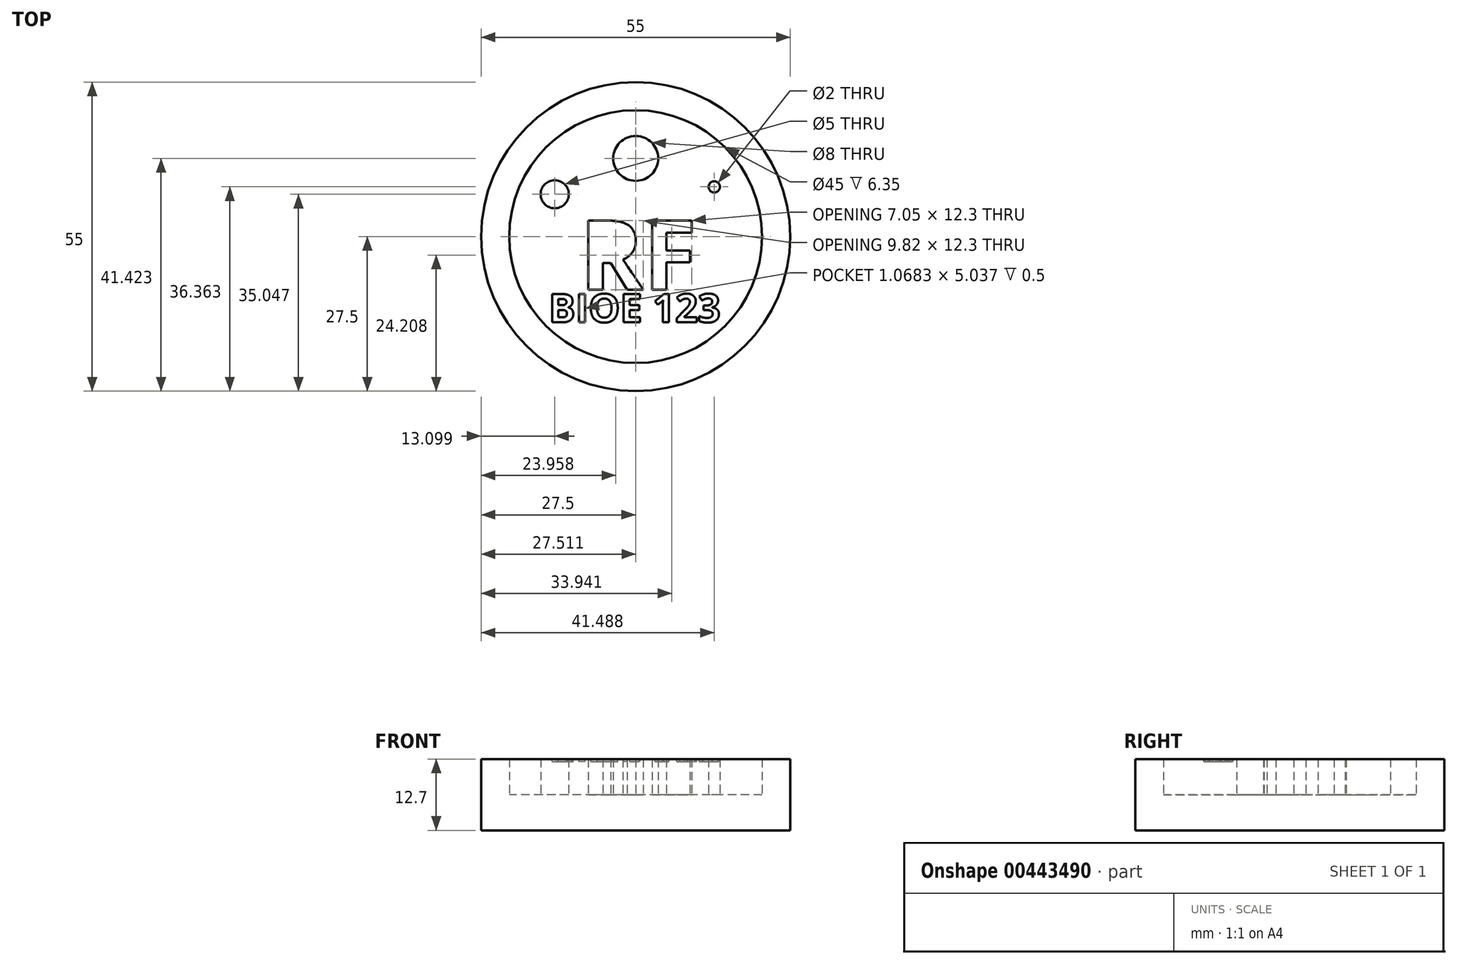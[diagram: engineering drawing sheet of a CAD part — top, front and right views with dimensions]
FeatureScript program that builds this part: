
annotation { "Feature Type Name" : "Feature", "Feature Type Description" : "" }
export const myFeature = defineFeature(function(context is Context, id is Id, definition is map)
    precondition{}
    {
        {
            var Q0;
            Q0=qCreatedBy(makeId("Top.planeOp"),FACE);
            var sketch = newSketch(context, id + "F0", { "sketchPlane" : qUnion([Q0])});
            skCircle(sketch, "E0", {"center": v(0, 0) * mm, "radius": 22.5 * mm});
            skCircle(sketch, "E1", {"center": v(0, 0) * mm, "radius": 27.5 * mm});
            skCircle(sketch, "E2", {"center": v(0.01, 13.92) * mm, "radius": 4 * mm});
            skCircle(sketch, "E3", {"center": v(-14.4, 7.55) * mm, "radius": 2.5 * mm});
            skCircle(sketch, "E4", {"center": v(13.99, 8.86) * mm, "radius": 1 * mm});
            skText(sketch, "E5", { "text": "RF", "fontName": "OpenSans-Bold.ttf"});
            const initialGuessF0  = {"E5": [-0.01, -0.00944, 1, 0, 0.0124]};
            skSetInitialGuess(sketch, initialGuessF0);
            skSolve(sketch);
        }
        {
            var Q0;
            Q0=makeQuery(id+"F0.imprint","IMPRINT",FACE,{"disambiguationData":[TD([[makeQuery(id+"F0.imprint","IMPRINT",EDGE,{"derivedFrom":sQuery(id+"F0.wireOp",EDGE,"E2")}),1.0]])]});
            var Q1;
            Q1=makeQuery(id+"F0.imprint","IMPRINT",FACE,{"disambiguationData":[TD([[makeQuery(id+"F0.imprint","IMPRINT",EDGE,{"derivedFrom":sQuery(id+"F0.wireOp",EDGE,"E4")}),1.0]])]});
            var Q2;
            Q2=makeQuery(id+"F0.imprint","IMPRINT",FACE,{"disambiguationData":[TD([[makeQuery(id+"F0.imprint","IMPRINT",EDGE,{"derivedFrom":sQuery(id+"F0.wireOp",EDGE,"E3")}),1.0]])]});
            var Q3;
            Q3=makeQuery(id+"F0.imprint","IMPRINT",FACE,{"disambiguationData":[TD([[makeQuery(id+"F0.imprint","IMPRINT",EDGE,{"derivedFrom":sQuery(id+"F0.wireOp",EDGE,"949e2ff5-e721-49a0-989e-4c56e190631b.sketch_text.stroke-0")}),-1.0]])]});
            var Q4;
            Q4=makeQuery(id+"F0.imprint","IMPRINT",FACE,{"disambiguationData":[TD([[makeQuery(id+"F0.imprint","IMPRINT",EDGE,{"derivedFrom":sQuery(id+"F0.wireOp",EDGE,"949e2ff5-e721-49a0-989e-4c56e190631b.sketch_text.stroke-26")}),-1.0]])]});
            var Q5;
            Q5=makeQuery(id+"F0.imprint","IMPRINT",FACE,{"disambiguationData":[TD([[makeQuery(id+"F0.imprint","IMPRINT",EDGE,{"derivedFrom":sQuery(id+"F0.wireOp",EDGE,"949e2ff5-e721-49a0-989e-4c56e190631b.sketch_text.stroke-19")}),-1.0]])]});
            var Q6;
            Q6=makeQuery(id+"F0.imprint","IMPRINT",FACE,{"disambiguationData":[TD([[makeQuery(id+"F0.imprint","IMPRINT",EDGE,{"derivedFrom":sQuery(id+"F0.wireOp",EDGE,"949e2ff5-e721-49a0-989e-4c56e190631b.sketch_text.stroke-36")}),-1.0]])]});
            var Q7;
            Q7=makeQuery(id+"F0.imprint","IMPRINT",FACE,{"disambiguationData":[TD([[makeQuery(id+"F0.imprint","IMPRINT",EDGE,{"derivedFrom":sQuery(id+"F0.wireOp",EDGE,"949e2ff5-e721-49a0-989e-4c56e190631b.sketch_text.stroke-40")}),-1.0]])]});
            var Q8;
            Q8=makeQuery(id+"F0.imprint","IMPRINT",FACE,{"disambiguationData":[TD([[makeQuery(id+"F0.imprint","IMPRINT",EDGE,{"derivedFrom":sQuery(id+"F0.wireOp",EDGE,"949e2ff5-e721-49a0-989e-4c56e190631b.sketch_text.stroke-48")}),-1.0]])]});
            var Q9;
            Q9=makeQuery(id+"F0.imprint","IMPRINT",FACE,{"disambiguationData":[TD([[makeQuery(id+"F0.imprint","IMPRINT",EDGE,{"derivedFrom":sQuery(id+"F0.wireOp",EDGE,"949e2ff5-e721-49a0-989e-4c56e190631b.sketch_text.stroke-110")}),-1.0]])]});
            var Q10;
            Q10=makeQuery(id+"F0.imprint","IMPRINT",FACE,{"disambiguationData":[TD([[makeQuery(id+"F0.imprint","IMPRINT",EDGE,{"derivedFrom":sQuery(id+"F0.wireOp",EDGE,"949e2ff5-e721-49a0-989e-4c56e190631b.sketch_text.stroke-122")}),-1.0]])]});
            var Q11;
            Q11=makeQuery(id+"F0.imprint","IMPRINT",FACE,{"disambiguationData":[TD([[makeQuery(id+"F0.imprint","IMPRINT",EDGE,{"derivedFrom":sQuery(id+"F0.wireOp",EDGE,"949e2ff5-e721-49a0-989e-4c56e190631b.sketch_text.stroke-100")}),-1.0]])]});
            var Q12;
            Q12=makeQuery(id+"F0.imprint","IMPRINT",FACE,{"disambiguationData":[TD([[makeQuery(id+"F0.imprint","IMPRINT",EDGE,{"derivedFrom":sQuery(id+"F0.wireOp",EDGE,"949e2ff5-e721-49a0-989e-4c56e190631b.sketch_text.stroke-88")}),-1.0]])]});
            var Q13;
            Q13=makeQuery(id+"F0.imprint","IMPRINT",FACE,{"disambiguationData":[TD([[makeQuery(id+"F0.imprint","IMPRINT",EDGE,{"derivedFrom":sQuery(id+"F0.wireOp",EDGE,"949e2ff5-e721-49a0-989e-4c56e190631b.sketch_text.stroke-92")}),-1.0]])]});
            var Q14;
            Q14=makeQuery(id+"F0.imprint","IMPRINT",FACE,{"disambiguationData":[TD([[makeQuery(id+"F0.imprint","IMPRINT",EDGE,{"derivedFrom":sQuery(id+"F0.wireOp",EDGE,"949e2ff5-e721-49a0-989e-4c56e190631b.sketch_text.stroke-63")}),-1.0]])]});
            var Q15;
            Q15=makeQuery(id+"F0.imprint","IMPRINT",FACE,{"disambiguationData":[TD([[makeQuery(id+"F0.imprint","IMPRINT",EDGE,{"derivedFrom":sQuery(id+"F0.wireOp",EDGE,"E5.sketch_text.stroke-0")}),1.0]])]});
            var Q16;
            Q16=makeQuery(id+"F0.imprint","IMPRINT",FACE,{"disambiguationData":[TD([[makeQuery(id+"F0.imprint","IMPRINT",EDGE,{"derivedFrom":sQuery(id+"F0.wireOp",EDGE,"E5.sketch_text.stroke-0")}),-1.0]])]});
            var Q17;
            Q17=makeQuery(id+"F0.imprint","IMPRINT",FACE,{"disambiguationData":[TD([[makeQuery(id+"F0.imprint","IMPRINT",EDGE,{"derivedFrom":sQuery(id+"F0.wireOp",EDGE,"E5.sketch_text.stroke-19")}),-1.0]])]});
            extrude(context, id + "F1", {"entities" : qUnion([Q0, Q1, Q2, Q3, Q4, Q5, Q6, Q7, Q8, Q9, Q10, Q11, Q12, Q13, Q14, Q15, Q16, Q17]), "depth" : 12.7 * mm});
        }
        {
            var Q0;
            Q0 = qSketchRegion(id + "F0", true);
            extrude(context, id + "F2", {"entities" : qUnion([Q0]), "operationType" : NewBodyOperationType.ADD, "depth" : 12.7 * mm});
        }
        {
            var Q0;
            Q0=makeQuery(id+"F0.imprint","IMPRINT",FACE,{"disambiguationData":[TD([[makeQuery(id+"F0.imprint","IMPRINT",EDGE,{"derivedFrom":sQuery(id+"F0.wireOp",EDGE,"E0")}),1.0]])]});
            extrude(context, id + "F3", {"entities" : qUnion([Q0]), "operationType" : NewBodyOperationType.ADD, "depth" : 6.35 * mm});
        }
        {
            var Q0;
            Q0=makeQuery(id+"F3.opExtrude","CAP_FACE",FACE,{"disambiguationData":[OSD([sQuery(id+"F0.wireOp",EDGE,"E0"),sQuery(id+"F0.wireOp",EDGE,"E2"),sQuery(id+"F0.wireOp",EDGE,"E3"),sQuery(id+"F0.wireOp",EDGE,"E4"),sQuery(id+"F0.wireOp",EDGE,"949e2ff5-e721-49a0-989e-4c56e190631b.sketch_text.stroke-0"),sQuery(id+"F0.wireOp",EDGE,"949e2ff5-e721-49a0-989e-4c56e190631b.sketch_text.stroke-1"),sQuery(id+"F0.wireOp",EDGE,"949e2ff5-e721-49a0-989e-4c56e190631b.sketch_text.stroke-2"),sQuery(id+"F0.wireOp",EDGE,"949e2ff5-e721-49a0-989e-4c56e190631b.sketch_text.stroke-3"),sQuery(id+"F0.wireOp",EDGE,"949e2ff5-e721-49a0-989e-4c56e190631b.sketch_text.stroke-4"),sQuery(id+"F0.wireOp",EDGE,"949e2ff5-e721-49a0-989e-4c56e190631b.sketch_text.stroke-5"),sQuery(id+"F0.wireOp",EDGE,"949e2ff5-e721-49a0-989e-4c56e190631b.sketch_text.stroke-6"),sQuery(id+"F0.wireOp",EDGE,"949e2ff5-e721-49a0-989e-4c56e190631b.sketch_text.stroke-7"),sQuery(id+"F0.wireOp",EDGE,"949e2ff5-e721-49a0-989e-4c56e190631b.sketch_text.stroke-8"),sQuery(id+"F0.wireOp",EDGE,"949e2ff5-e721-49a0-989e-4c56e190631b.sketch_text.stroke-9"),sQuery(id+"F0.wireOp",EDGE,"949e2ff5-e721-49a0-989e-4c56e190631b.sketch_text.stroke-10"),sQuery(id+"F0.wireOp",EDGE,"949e2ff5-e721-49a0-989e-4c56e190631b.sketch_text.stroke-11"),sQuery(id+"F0.wireOp",EDGE,"949e2ff5-e721-49a0-989e-4c56e190631b.sketch_text.stroke-12"),sQuery(id+"F0.wireOp",EDGE,"949e2ff5-e721-49a0-989e-4c56e190631b.sketch_text.stroke-13"),sQuery(id+"F0.wireOp",EDGE,"949e2ff5-e721-49a0-989e-4c56e190631b.sketch_text.stroke-19"),sQuery(id+"F0.wireOp",EDGE,"949e2ff5-e721-49a0-989e-4c56e190631b.sketch_text.stroke-20"),sQuery(id+"F0.wireOp",EDGE,"949e2ff5-e721-49a0-989e-4c56e190631b.sketch_text.stroke-21"),sQuery(id+"F0.wireOp",EDGE,"949e2ff5-e721-49a0-989e-4c56e190631b.sketch_text.stroke-22"),sQuery(id+"F0.wireOp",EDGE,"949e2ff5-e721-49a0-989e-4c56e190631b.sketch_text.stroke-23"),sQuery(id+"F0.wireOp",EDGE,"949e2ff5-e721-49a0-989e-4c56e190631b.sketch_text.stroke-24"),sQuery(id+"F0.wireOp",EDGE,"949e2ff5-e721-49a0-989e-4c56e190631b.sketch_text.stroke-25"),sQuery(id+"F0.wireOp",EDGE,"949e2ff5-e721-49a0-989e-4c56e190631b.sketch_text.stroke-26"),sQuery(id+"F0.wireOp",EDGE,"949e2ff5-e721-49a0-989e-4c56e190631b.sketch_text.stroke-27"),sQuery(id+"F0.wireOp",EDGE,"949e2ff5-e721-49a0-989e-4c56e190631b.sketch_text.stroke-28"),sQuery(id+"F0.wireOp",EDGE,"949e2ff5-e721-49a0-989e-4c56e190631b.sketch_text.stroke-29"),sQuery(id+"F0.wireOp",EDGE,"949e2ff5-e721-49a0-989e-4c56e190631b.sketch_text.stroke-30"),sQuery(id+"F0.wireOp",EDGE,"949e2ff5-e721-49a0-989e-4c56e190631b.sketch_text.stroke-31"),sQuery(id+"F0.wireOp",EDGE,"949e2ff5-e721-49a0-989e-4c56e190631b.sketch_text.stroke-32"),sQuery(id+"F0.wireOp",EDGE,"949e2ff5-e721-49a0-989e-4c56e190631b.sketch_text.stroke-33"),sQuery(id+"F0.wireOp",EDGE,"949e2ff5-e721-49a0-989e-4c56e190631b.sketch_text.stroke-34"),sQuery(id+"F0.wireOp",EDGE,"949e2ff5-e721-49a0-989e-4c56e190631b.sketch_text.stroke-35"),sQuery(id+"F0.wireOp",EDGE,"949e2ff5-e721-49a0-989e-4c56e190631b.sketch_text.stroke-36"),sQuery(id+"F0.wireOp",EDGE,"949e2ff5-e721-49a0-989e-4c56e190631b.sketch_text.stroke-37"),sQuery(id+"F0.wireOp",EDGE,"949e2ff5-e721-49a0-989e-4c56e190631b.sketch_text.stroke-38"),sQuery(id+"F0.wireOp",EDGE,"949e2ff5-e721-49a0-989e-4c56e190631b.sketch_text.stroke-39"),sQuery(id+"F0.wireOp",EDGE,"949e2ff5-e721-49a0-989e-4c56e190631b.sketch_text.stroke-40"),sQuery(id+"F0.wireOp",EDGE,"949e2ff5-e721-49a0-989e-4c56e190631b.sketch_text.stroke-41"),sQuery(id+"F0.wireOp",EDGE,"949e2ff5-e721-49a0-989e-4c56e190631b.sketch_text.stroke-42"),sQuery(id+"F0.wireOp",EDGE,"949e2ff5-e721-49a0-989e-4c56e190631b.sketch_text.stroke-43"),sQuery(id+"F0.wireOp",EDGE,"949e2ff5-e721-49a0-989e-4c56e190631b.sketch_text.stroke-44"),sQuery(id+"F0.wireOp",EDGE,"949e2ff5-e721-49a0-989e-4c56e190631b.sketch_text.stroke-45"),sQuery(id+"F0.wireOp",EDGE,"949e2ff5-e721-49a0-989e-4c56e190631b.sketch_text.stroke-46"),sQuery(id+"F0.wireOp",EDGE,"949e2ff5-e721-49a0-989e-4c56e190631b.sketch_text.stroke-47"),sQuery(id+"F0.wireOp",EDGE,"949e2ff5-e721-49a0-989e-4c56e190631b.sketch_text.stroke-48"),sQuery(id+"F0.wireOp",EDGE,"949e2ff5-e721-49a0-989e-4c56e190631b.sketch_text.stroke-49"),sQuery(id+"F0.wireOp",EDGE,"949e2ff5-e721-49a0-989e-4c56e190631b.sketch_text.stroke-50"),sQuery(id+"F0.wireOp",EDGE,"949e2ff5-e721-49a0-989e-4c56e190631b.sketch_text.stroke-51"),sQuery(id+"F0.wireOp",EDGE,"949e2ff5-e721-49a0-989e-4c56e190631b.sketch_text.stroke-52"),sQuery(id+"F0.wireOp",EDGE,"949e2ff5-e721-49a0-989e-4c56e190631b.sketch_text.stroke-53"),sQuery(id+"F0.wireOp",EDGE,"949e2ff5-e721-49a0-989e-4c56e190631b.sketch_text.stroke-54"),sQuery(id+"F0.wireOp",EDGE,"949e2ff5-e721-49a0-989e-4c56e190631b.sketch_text.stroke-55"),sQuery(id+"F0.wireOp",EDGE,"949e2ff5-e721-49a0-989e-4c56e190631b.sketch_text.stroke-56"),sQuery(id+"F0.wireOp",EDGE,"949e2ff5-e721-49a0-989e-4c56e190631b.sketch_text.stroke-57"),sQuery(id+"F0.wireOp",EDGE,"949e2ff5-e721-49a0-989e-4c56e190631b.sketch_text.stroke-58"),sQuery(id+"F0.wireOp",EDGE,"949e2ff5-e721-49a0-989e-4c56e190631b.sketch_text.stroke-59"),sQuery(id+"F0.wireOp",EDGE,"949e2ff5-e721-49a0-989e-4c56e190631b.sketch_text.stroke-60"),sQuery(id+"F0.wireOp",EDGE,"949e2ff5-e721-49a0-989e-4c56e190631b.sketch_text.stroke-61"),sQuery(id+"F0.wireOp",EDGE,"949e2ff5-e721-49a0-989e-4c56e190631b.sketch_text.stroke-62"),sQuery(id+"F0.wireOp",EDGE,"949e2ff5-e721-49a0-989e-4c56e190631b.sketch_text.stroke-63"),sQuery(id+"F0.wireOp",EDGE,"949e2ff5-e721-49a0-989e-4c56e190631b.sketch_text.stroke-64"),sQuery(id+"F0.wireOp",EDGE,"949e2ff5-e721-49a0-989e-4c56e190631b.sketch_text.stroke-65"),sQuery(id+"F0.wireOp",EDGE,"949e2ff5-e721-49a0-989e-4c56e190631b.sketch_text.stroke-66"),sQuery(id+"F0.wireOp",EDGE,"949e2ff5-e721-49a0-989e-4c56e190631b.sketch_text.stroke-67"),sQuery(id+"F0.wireOp",EDGE,"949e2ff5-e721-49a0-989e-4c56e190631b.sketch_text.stroke-68"),sQuery(id+"F0.wireOp",EDGE,"949e2ff5-e721-49a0-989e-4c56e190631b.sketch_text.stroke-69"),sQuery(id+"F0.wireOp",EDGE,"949e2ff5-e721-49a0-989e-4c56e190631b.sketch_text.stroke-70"),sQuery(id+"F0.wireOp",EDGE,"949e2ff5-e721-49a0-989e-4c56e190631b.sketch_text.stroke-71"),sQuery(id+"F0.wireOp",EDGE,"949e2ff5-e721-49a0-989e-4c56e190631b.sketch_text.stroke-72"),sQuery(id+"F0.wireOp",EDGE,"949e2ff5-e721-49a0-989e-4c56e190631b.sketch_text.stroke-73"),sQuery(id+"F0.wireOp",EDGE,"949e2ff5-e721-49a0-989e-4c56e190631b.sketch_text.stroke-74"),sQuery(id+"F0.wireOp",EDGE,"949e2ff5-e721-49a0-989e-4c56e190631b.sketch_text.stroke-75"),sQuery(id+"F0.wireOp",EDGE,"949e2ff5-e721-49a0-989e-4c56e190631b.sketch_text.stroke-76"),sQuery(id+"F0.wireOp",EDGE,"949e2ff5-e721-49a0-989e-4c56e190631b.sketch_text.stroke-77"),sQuery(id+"F0.wireOp",EDGE,"949e2ff5-e721-49a0-989e-4c56e190631b.sketch_text.stroke-78"),sQuery(id+"F0.wireOp",EDGE,"949e2ff5-e721-49a0-989e-4c56e190631b.sketch_text.stroke-88"),sQuery(id+"F0.wireOp",EDGE,"949e2ff5-e721-49a0-989e-4c56e190631b.sketch_text.stroke-89"),sQuery(id+"F0.wireOp",EDGE,"949e2ff5-e721-49a0-989e-4c56e190631b.sketch_text.stroke-90"),sQuery(id+"F0.wireOp",EDGE,"949e2ff5-e721-49a0-989e-4c56e190631b.sketch_text.stroke-91"),sQuery(id+"F0.wireOp",EDGE,"949e2ff5-e721-49a0-989e-4c56e190631b.sketch_text.stroke-92"),sQuery(id+"F0.wireOp",EDGE,"949e2ff5-e721-49a0-989e-4c56e190631b.sketch_text.stroke-93"),sQuery(id+"F0.wireOp",EDGE,"949e2ff5-e721-49a0-989e-4c56e190631b.sketch_text.stroke-94"),sQuery(id+"F0.wireOp",EDGE,"949e2ff5-e721-49a0-989e-4c56e190631b.sketch_text.stroke-95"),sQuery(id+"F0.wireOp",EDGE,"949e2ff5-e721-49a0-989e-4c56e190631b.sketch_text.stroke-96"),sQuery(id+"F0.wireOp",EDGE,"949e2ff5-e721-49a0-989e-4c56e190631b.sketch_text.stroke-97"),sQuery(id+"F0.wireOp",EDGE,"949e2ff5-e721-49a0-989e-4c56e190631b.sketch_text.stroke-98"),sQuery(id+"F0.wireOp",EDGE,"949e2ff5-e721-49a0-989e-4c56e190631b.sketch_text.stroke-99"),sQuery(id+"F0.wireOp",EDGE,"949e2ff5-e721-49a0-989e-4c56e190631b.sketch_text.stroke-100"),sQuery(id+"F0.wireOp",EDGE,"949e2ff5-e721-49a0-989e-4c56e190631b.sketch_text.stroke-101"),sQuery(id+"F0.wireOp",EDGE,"949e2ff5-e721-49a0-989e-4c56e190631b.sketch_text.stroke-102"),sQuery(id+"F0.wireOp",EDGE,"949e2ff5-e721-49a0-989e-4c56e190631b.sketch_text.stroke-103"),sQuery(id+"F0.wireOp",EDGE,"949e2ff5-e721-49a0-989e-4c56e190631b.sketch_text.stroke-104"),sQuery(id+"F0.wireOp",EDGE,"949e2ff5-e721-49a0-989e-4c56e190631b.sketch_text.stroke-105"),sQuery(id+"F0.wireOp",EDGE,"949e2ff5-e721-49a0-989e-4c56e190631b.sketch_text.stroke-106"),sQuery(id+"F0.wireOp",EDGE,"949e2ff5-e721-49a0-989e-4c56e190631b.sketch_text.stroke-107"),sQuery(id+"F0.wireOp",EDGE,"949e2ff5-e721-49a0-989e-4c56e190631b.sketch_text.stroke-108"),sQuery(id+"F0.wireOp",EDGE,"949e2ff5-e721-49a0-989e-4c56e190631b.sketch_text.stroke-109"),sQuery(id+"F0.wireOp",EDGE,"949e2ff5-e721-49a0-989e-4c56e190631b.sketch_text.stroke-110"),sQuery(id+"F0.wireOp",EDGE,"949e2ff5-e721-49a0-989e-4c56e190631b.sketch_text.stroke-111"),sQuery(id+"F0.wireOp",EDGE,"949e2ff5-e721-49a0-989e-4c56e190631b.sketch_text.stroke-112"),sQuery(id+"F0.wireOp",EDGE,"949e2ff5-e721-49a0-989e-4c56e190631b.sketch_text.stroke-113"),sQuery(id+"F0.wireOp",EDGE,"949e2ff5-e721-49a0-989e-4c56e190631b.sketch_text.stroke-114"),sQuery(id+"F0.wireOp",EDGE,"949e2ff5-e721-49a0-989e-4c56e190631b.sketch_text.stroke-115"),sQuery(id+"F0.wireOp",EDGE,"949e2ff5-e721-49a0-989e-4c56e190631b.sketch_text.stroke-116"),sQuery(id+"F0.wireOp",EDGE,"949e2ff5-e721-49a0-989e-4c56e190631b.sketch_text.stroke-117"),sQuery(id+"F0.wireOp",EDGE,"949e2ff5-e721-49a0-989e-4c56e190631b.sketch_text.stroke-118"),sQuery(id+"F0.wireOp",EDGE,"949e2ff5-e721-49a0-989e-4c56e190631b.sketch_text.stroke-119"),sQuery(id+"F0.wireOp",EDGE,"949e2ff5-e721-49a0-989e-4c56e190631b.sketch_text.stroke-120"),sQuery(id+"F0.wireOp",EDGE,"949e2ff5-e721-49a0-989e-4c56e190631b.sketch_text.stroke-121"),sQuery(id+"F0.wireOp",EDGE,"949e2ff5-e721-49a0-989e-4c56e190631b.sketch_text.stroke-122"),sQuery(id+"F0.wireOp",EDGE,"949e2ff5-e721-49a0-989e-4c56e190631b.sketch_text.stroke-123"),sQuery(id+"F0.wireOp",EDGE,"949e2ff5-e721-49a0-989e-4c56e190631b.sketch_text.stroke-124"),sQuery(id+"F0.wireOp",EDGE,"949e2ff5-e721-49a0-989e-4c56e190631b.sketch_text.stroke-125"),sQuery(id+"F0.wireOp",EDGE,"949e2ff5-e721-49a0-989e-4c56e190631b.sketch_text.stroke-126"),sQuery(id+"F0.wireOp",EDGE,"949e2ff5-e721-49a0-989e-4c56e190631b.sketch_text.stroke-127"),sQuery(id+"F0.wireOp",EDGE,"949e2ff5-e721-49a0-989e-4c56e190631b.sketch_text.stroke-128"),sQuery(id+"F0.wireOp",EDGE,"949e2ff5-e721-49a0-989e-4c56e190631b.sketch_text.stroke-129"),sQuery(id+"F0.wireOp",EDGE,"949e2ff5-e721-49a0-989e-4c56e190631b.sketch_text.stroke-130")])],"isStart":false});
            extrude(context, id + "F4", {"entities" : qUnion([Q0]), "depth" : 6.35 * mm});
        }
        {
            var Q0;
            Q0=makeQuery(id+"F4.opExtrude","CAP_FACE",FACE,{"disambiguationData":[OSD([sQuery(id+"F0.wireOp",EDGE,"E0"),sQuery(id+"F0.wireOp",EDGE,"E2"),sQuery(id+"F0.wireOp",EDGE,"E3"),sQuery(id+"F0.wireOp",EDGE,"E4"),sQuery(id+"F0.wireOp",EDGE,"E5.sketch_text.stroke-7"),sQuery(id+"F0.wireOp",EDGE,"E5.sketch_text.stroke-8"),sQuery(id+"F0.wireOp",EDGE,"E5.sketch_text.stroke-9"),sQuery(id+"F0.wireOp",EDGE,"E5.sketch_text.stroke-10"),sQuery(id+"F0.wireOp",EDGE,"E5.sketch_text.stroke-11"),sQuery(id+"F0.wireOp",EDGE,"E5.sketch_text.stroke-12"),sQuery(id+"F0.wireOp",EDGE,"E5.sketch_text.stroke-13"),sQuery(id+"F0.wireOp",EDGE,"E5.sketch_text.stroke-14"),sQuery(id+"F0.wireOp",EDGE,"E5.sketch_text.stroke-15"),sQuery(id+"F0.wireOp",EDGE,"E5.sketch_text.stroke-16"),sQuery(id+"F0.wireOp",EDGE,"E5.sketch_text.stroke-17"),sQuery(id+"F0.wireOp",EDGE,"E5.sketch_text.stroke-18"),sQuery(id+"F0.wireOp",EDGE,"E5.sketch_text.stroke-19"),sQuery(id+"F0.wireOp",EDGE,"E5.sketch_text.stroke-20"),sQuery(id+"F0.wireOp",EDGE,"E5.sketch_text.stroke-21"),sQuery(id+"F0.wireOp",EDGE,"E5.sketch_text.stroke-22"),sQuery(id+"F0.wireOp",EDGE,"E5.sketch_text.stroke-23"),sQuery(id+"F0.wireOp",EDGE,"E5.sketch_text.stroke-24"),sQuery(id+"F0.wireOp",EDGE,"E5.sketch_text.stroke-25"),sQuery(id+"F0.wireOp",EDGE,"E5.sketch_text.stroke-26"),sQuery(id+"F0.wireOp",EDGE,"E5.sketch_text.stroke-27"),sQuery(id+"F0.wireOp",EDGE,"E5.sketch_text.stroke-28")])],"isStart":false});
            var sketch = newSketch(context, id + "F5", { "sketchPlane" : qUnion([Q0])});
            skText(sketch, "E6", { "text": "BIOE 123", "fontName": "OpenSans-Bold.ttf"});
            const initialGuessF5  = {"E6": [-0.01547, -0.01525, 1, 0, 0.00508]};
            skSetInitialGuess(sketch, initialGuessF5);
            skSolve(sketch);
        }
        {
            var Q0;
            Q0 = qSketchRegion(id + "F5", true);
            extrude(context, id + "F6", {"entities" : qUnion([Q0]), "operationType" : NewBodyOperationType.REMOVE, "oppositeDirection" : true, "depth" : .5 * mm});
        }
    });
